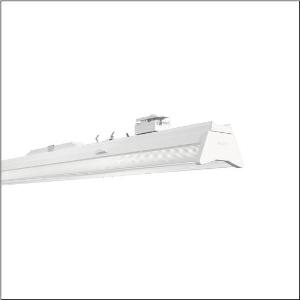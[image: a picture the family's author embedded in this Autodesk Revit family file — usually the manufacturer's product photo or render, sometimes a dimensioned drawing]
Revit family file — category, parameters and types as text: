
# Revit family: licross_r__21_performance_mo_52td167n445g_3390
name_source: partatom
category: Lighting Fixtures
units: mm (PartAtom-declared; Revit-internal decimal feet)

## family parameters
Cut with Voids When Loaded = No
Host = Face
Light Source = No
Part Type = Normal
Room Calculation Point = No
Round Connector Dimension = Use Diameter
Shared = No

## types (1)
- Licross® 21 Performance MO (1 x LED, 4580 lm, 24.7 W, 4000K)
    Apparent Load = 25 VA
    CIE Flux Codes = 66 88 96 79 100
    Color Rendering = 80
    Color Temperature = 4000K
    Default Elevation = 1800 mm
    Description = Licross® 21 Performance MO, luminaire insert, of sheet steel, galvanised, coil coated, white, length: 1.500mm, width: 120mm, height: 123mm, LED rated luminous flux: 4.580lm, light colour: 840, SDCM (Standard Deviation of Colour Matching)MacAdam ≤ 3 SDCM (initial), control gear: ON/OFF, with plug, 3-pole, with phase selection, mains connection: 220..240V, AC, 50/60Hz, rated input power: 25W, internal wiring halogen-free, primary light control with lens, of plastic, primary optical cover: cover, of PMMA, CAT 2 (L<= 3000cd/m²), light emission: direct/indirect distribution, primary light characteristic: symmetric, protection rating (complete): IP54, insulation class (complete): insulation class I (protective earthing), certification: CE, ENEC, UKCA, protection symbol: D if used in an environment with non-conductive dust loads with corresponding accessories, impact resistance: IK06, permissible ambient temperature for indoor applications: -35..+55°C, corresponds to IFS (International Featured Standards) requirements for safety and quality in the food industry, reducing of maximum allowable ambient temperature of 5°C with ceiling mounting, LABS conformity tested according to VDMA 24364:2018-05, packaging unit: 1 piece
    Height = 114 mm
    Lamp = 1 x LED
    Lamp Light Flux = 4580 lm
    Lamp Power = 24.7 W
    Lamp count = 1
    Length = 1500 mm
    Luminous efficacy = 185 lm/W
    Manufacturer = Siteco
    ModVariant = No
    Model = 52TD167N445G
    Mounting Place = Ceiling
    Mounting Type = Pendant
    Number of Poles = 1
    OnlyDefault = Yes
    Power Factor = 1
    Product Name = Licross® 21 Performance MO
    Product group = luminaire insert | ceiling pendant
    ProductGroupID = 901
    Protection Class = Protection class I
    Protection Degree = IP 54
    RLX_Detail_Level = 1
    RLX_Emergency_Light_Flux = 0 lm
    RLX_Emergency_Type = 0
    RLX_Emergency_Type_DB = No
    RlxData = <blob elided: 30561 chars, md5=1e8cfd02>
    Socket = socket
    Standby Power = 0 W
    System Light Flux = 4580 lm
    System Power = 25 W
    Type Comments = Product without accessories
    Type Image = l_1256138.jpg
    URL = http://relux.com
    VarID = ---
    Voltage = 0 V
    Weight = 0.00 kg
    Width = 120 mm

## geometry (parser evidence)
native form markers: Blend x4, Sweep x14
no freeform markers — native parametric forms only
